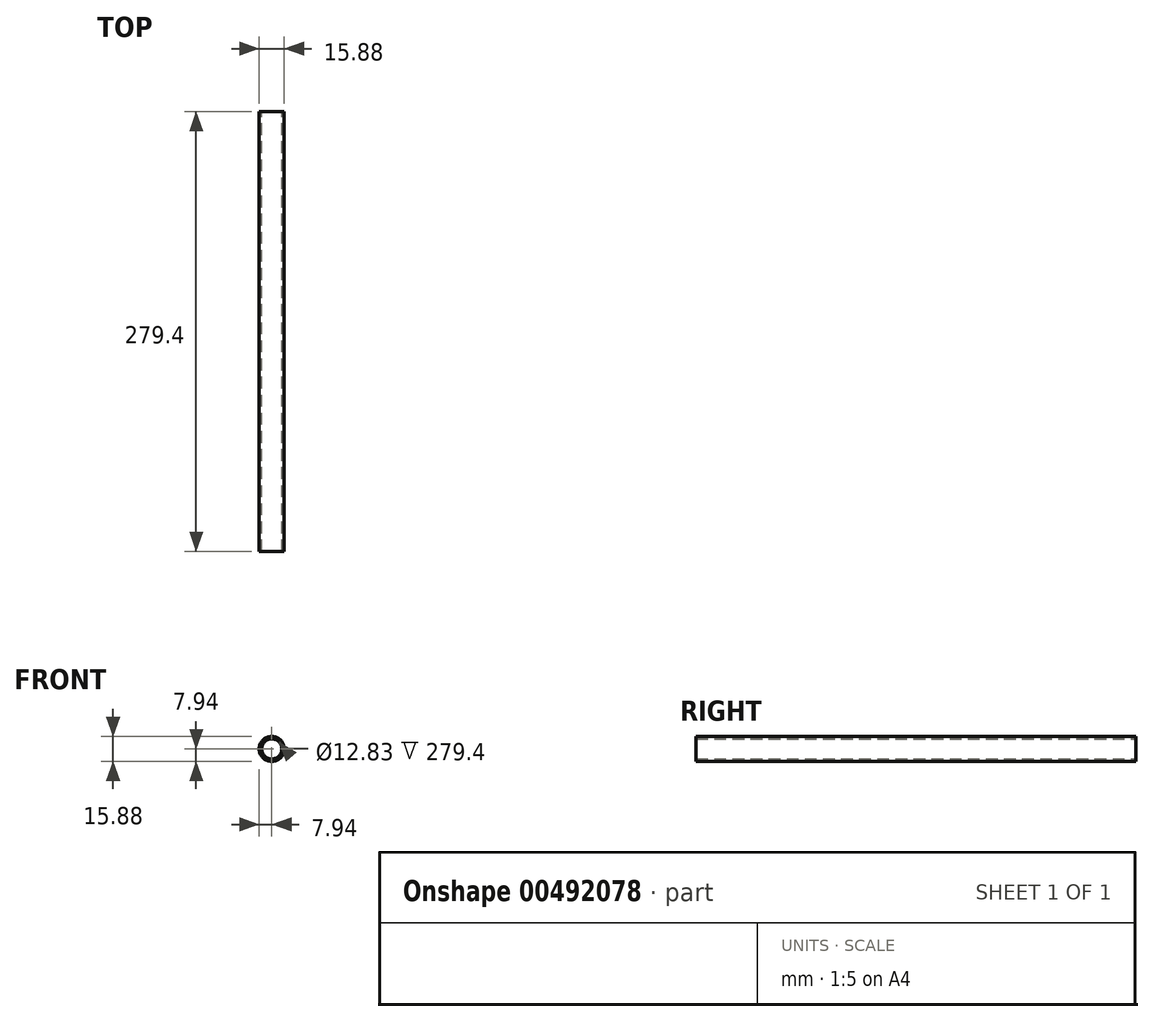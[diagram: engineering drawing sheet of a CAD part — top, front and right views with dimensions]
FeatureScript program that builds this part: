
annotation { "Feature Type Name" : "Feature", "Feature Type Description" : "" }
export const myFeature = defineFeature(function(context is Context, id is Id, definition is map)
    precondition{}
    {
        {
            var Q0;
            Q0=qCreatedBy(makeId("Front.planeOp"),FACE);
            var sketch = newSketch(context, id + "F0", { "sketchPlane" : qUnion([Q0])});
            skCircle(sketch, "E0", {"center": v(0, 0) * mm, "radius": 7.94 * mm});
            skCircle(sketch, "E1", {"center": v(0, 0) * mm, "radius": 6.41 * mm});
            skSolve(sketch);
        }
        {
            var Q0;
            Q0=makeQuery(id+"F0.imprint","IMPRINT",FACE,{"disambiguationData":[TD([[makeQuery(id+"F0.imprint","IMPRINT",EDGE,{"derivedFrom":sQuery(id+"F0.wireOp",EDGE,"E0")}),1.0]])]});
            extrude(context, id + "F1", {"entities" : qUnion([Q0]), "depth" : 279.4 * mm});
        }
    });
